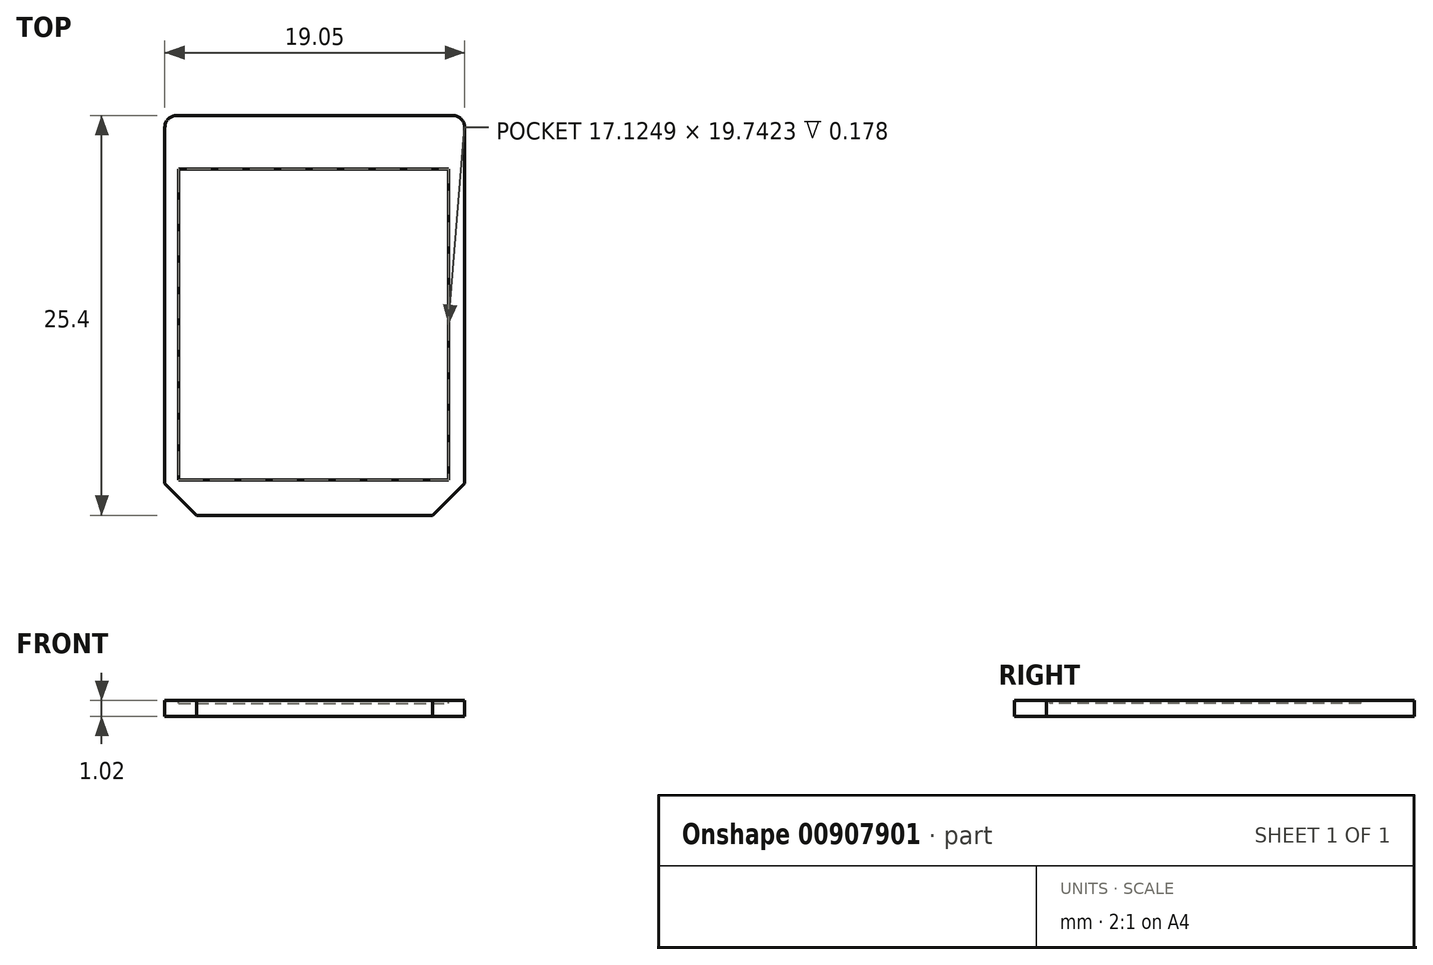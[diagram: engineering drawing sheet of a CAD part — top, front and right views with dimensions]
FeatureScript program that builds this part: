
annotation { "Feature Type Name" : "Feature", "Feature Type Description" : "" }
export const myFeature = defineFeature(function(context is Context, id is Id, definition is map)
    precondition{}
    {
        {
            var Q0;
            Q0=qCreatedBy(makeId("Top.planeOp"),FACE);
            var sketch = newSketch(context, id + "F0", { "sketchPlane" : qUnion([Q0])});
            skLineSegment(sketch, "E0.bottom", {"start": v(0, 0) * mm, "end": v(19.05, 0) * mm});
            skLineSegment(sketch, "E0.top", {"start": v(0, 25.4) * mm, "end": v(19.05, 25.4) * mm});
            skLineSegment(sketch, "E0.left", {"start": v(0, 0) * mm, "end": v(0, 25.4) * mm});
            skLineSegment(sketch, "E0.right", {"start": v(19.05, 0) * mm, "end": v(19.05, 25.4) * mm});
            skSolve(sketch);
        }
        {
            var Q0;
            Q0=makeQuery(id+"F0.imprint","IMPRINT",FACE,{"disambiguationData":[TD([[makeQuery(id+"F0.imprint","IMPRINT",EDGE,{"derivedFrom":sQuery(id+"F0.wireOp",EDGE,"E0.bottom")}),1.0]])]});
            extrude(context, id + "F1", {"entities" : qUnion([Q0]), "depth" : 1.02 * mm, "offsetDistance" : 25.4 * mm});
        }
        {
            var Q0;
            Q0=makeQuery(id+"F1.opExtrude","SWEPT_EDGE",EDGE,{"disambiguationData":[OSD([sQuery(id+"F0.wireOp",EDGE,"E0.bottom"),sQuery(id+"F0.wireOp",EDGE,"E0.left")])]});
            chamfer(context, id + "F2", {"entities" : qUnion([Q0]), "width" : 2.03 * mm, "tangentPropagation" : true});
        }
        {
            var Q0;
            Q0=makeQuery(id+"F1.opExtrude","SWEPT_EDGE",EDGE,{"disambiguationData":[OSD([sQuery(id+"F0.wireOp",EDGE,"E0.bottom"),sQuery(id+"F0.wireOp",EDGE,"E0.right")])]});
            chamfer(context, id + "F3", {"entities" : qUnion([Q0]), "width" : 2.03 * mm, "tangentPropagation" : true});
        }
        {
            var Q0;
            Q0=makeQuery(id+"F1.opExtrude","SWEPT_EDGE",EDGE,{"disambiguationData":[OSD([sQuery(id+"F0.wireOp",EDGE,"E0.top"),sQuery(id+"F0.wireOp",EDGE,"E0.right")])]});
            fillet(context, id + "F4", {"entities" : qUnion([Q0]), "radius" : 0.76 * mm, "tangentPropagation" : true, "allowEdgeOverflow" : false});
        }
        {
            var Q0;
            Q0=makeQuery(id+"F1.opExtrude","SWEPT_EDGE",EDGE,{"disambiguationData":[OSD([sQuery(id+"F0.wireOp",EDGE,"E0.top"),sQuery(id+"F0.wireOp",EDGE,"E0.left")])]});
            fillet(context, id + "F5", {"entities" : qUnion([Q0]), "radius" : 0.76 * mm, "tangentPropagation" : true, "allowEdgeOverflow" : false});
        }
        {
            var Q0;
            Q0=makeQuery(id+"F1.opExtrude","CAP_FACE",FACE,{"disambiguationData":[OSD([sQuery(id+"F0.wireOp",EDGE,"E0.bottom"),sQuery(id+"F0.wireOp",EDGE,"E0.top"),sQuery(id+"F0.wireOp",EDGE,"E0.left"),sQuery(id+"F0.wireOp",EDGE,"E0.right")])],"isStart":false});
            var sketch = newSketch(context, id + "F6", { "sketchPlane" : qUnion([Q0])});
            skLineSegment(sketch, "E1.bottom", {"start": v(0.89, 22) * mm, "end": v(18.01, 22) * mm});
            skLineSegment(sketch, "E1.top", {"start": v(0.89, 2.26) * mm, "end": v(18.01, 2.26) * mm});
            skLineSegment(sketch, "E1.left", {"start": v(0.89, 22) * mm, "end": v(0.89, 2.26) * mm});
            skLineSegment(sketch, "E1.right", {"start": v(18.01, 22) * mm, "end": v(18.01, 2.26) * mm});
            skSolve(sketch);
        }
        {
            var Q0;
            Q0=qSketchRegion(id+"F6",true);
            extrude(context, id + "F7", {"entities" : qUnion([Q0]), "operationType" : NewBodyOperationType.REMOVE, "oppositeDirection" : true, "depth" : 0.18 * mm, "offsetDistance" : 25.4 * mm});
        }
    });
